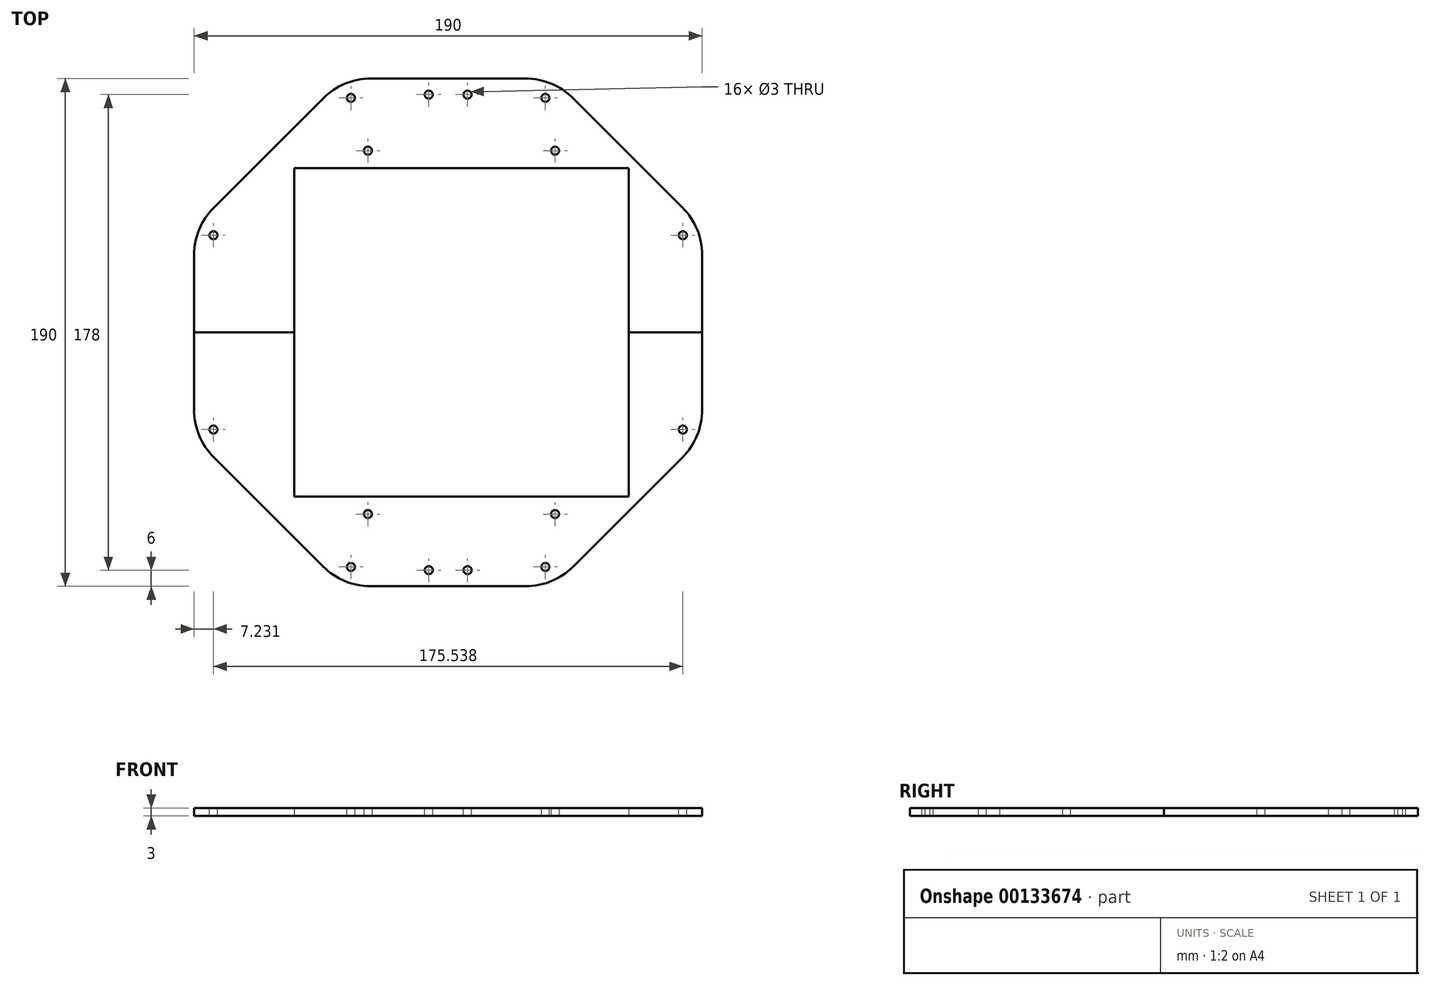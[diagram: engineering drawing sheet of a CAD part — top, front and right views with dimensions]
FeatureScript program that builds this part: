
annotation { "Feature Type Name" : "Feature", "Feature Type Description" : "" }
export const myFeature = defineFeature(function(context is Context, id is Id, definition is map)
    precondition{}
    {
        {
            var Q0;
            Q0=qCreatedBy(makeId("Top.planeOp"),FACE);
            var sketch = newSketch(context, id + "F0", { "sketchPlane" : qUnion([Q0])});
            skCircle(sketch, "E0.cCircle", {"center": v(0, 0) * mm, "radius": 95 * mm, "construction": true});
            skLineSegment(sketch, "E0.0", {"start": v(-95, -39.35) * mm, "end": v(-95, 39.35) * mm});
            skLineSegment(sketch, "E0.1", {"start": v(-95, 39.35) * mm, "end": v(-39.35, 95) * mm});
            skLineSegment(sketch, "E0.2", {"start": v(-39.35, 95) * mm, "end": v(39.35, 95) * mm});
            skLineSegment(sketch, "E0.3", {"start": v(39.35, 95) * mm, "end": v(95, 39.35) * mm});
            skLineSegment(sketch, "E0.4", {"start": v(95, 39.35) * mm, "end": v(95, -39.35) * mm});
            skLineSegment(sketch, "E0.5", {"start": v(95, -39.35) * mm, "end": v(39.35, -95) * mm});
            skLineSegment(sketch, "E0.6", {"start": v(39.35, -95) * mm, "end": v(-39.35, -95) * mm});
            skLineSegment(sketch, "E0.7", {"start": v(-39.35, -95) * mm, "end": v(-95, -39.35) * mm});
            skPoint(sketch, "E0.0.midPoint", {"position": v(-95, 0) * mm});
            skLineSegment(sketch, "E1.0", {"start": v(-91, -37.7) * mm, "end": v(-91, 37.7) * mm});
            skLineSegment(sketch, "E1.1", {"start": v(-37.7, -91) * mm, "end": v(-91, -37.7) * mm});
            skLineSegment(sketch, "E1.2", {"start": v(-91, 37.7) * mm, "end": v(-37.7, 91) * mm});
            skLineSegment(sketch, "E1.3", {"start": v(37.7, -91) * mm, "end": v(-37.7, -91) * mm});
            skLineSegment(sketch, "E1.4", {"start": v(-37.7, 91) * mm, "end": v(37.7, 91) * mm});
            skLineSegment(sketch, "E1.5", {"start": v(37.7, 91) * mm, "end": v(91, 37.7) * mm});
            skLineSegment(sketch, "E1.6", {"start": v(91, 37.7) * mm, "end": v(91, -37.7) * mm});
            skLineSegment(sketch, "E1.7", {"start": v(91, -37.7) * mm, "end": v(37.7, -91) * mm});
            skLineSegment(sketch, "E2", {"start": v(0, 91) * mm, "end": v(0, 95) * mm});
            skLineSegment(sketch, "E3", {"start": v(-95, 0) * mm, "end": v(95, 0) * mm});
            skLineSegment(sketch, "E4", {"start": v(0, -91) * mm, "end": v(0, -95) * mm});
            skCircle(sketch, "E5", {"center": v(-87.77, 36.36) * mm, "radius": 1.5 * mm});
            skCircle(sketch, "E6", {"center": v(-7.25, 89) * mm, "radius": 1.5 * mm});
            skCircle(sketch, "E7", {"center": v(7.25, 89) * mm, "radius": 1.5 * mm});
            skLineSegment(sketch, "E8", {"start": v(0, 0) * mm, "end": v(-95, 39.35) * mm, "construction": true});
            skLineSegment(sketch, "E9", {"start": v(0, 0) * mm, "end": v(0, 89) * mm, "construction": true});
            skLineSegment(sketch, "E10", {"start": v(-7.25, 89) * mm, "end": v(0, 89) * mm, "construction": true});
            skLineSegment(sketch, "E11", {"start": v(7.25, 89) * mm, "end": v(0, 89) * mm, "construction": true});
            skArc(sketch, "E12", {"start": v(-15.77, 91) * mm, "mid": v(-7.25, 85.59) * mm, "end": v(1.27, 91) * mm});
            skArc(sketch, "E13", {"start": v(-1.27, 91) * mm, "mid": v(7.25, 85.59) * mm, "end": v(15.77, 91) * mm});
            skLineSegment(sketch, "E14", {"start": v(0, 89) * mm, "end": v(0, 91) * mm});
            skArc(sketch, "E15.1.0", {"start": v(15.77, -91) * mm, "mid": v(7.25, -85.59) * mm, "end": v(-1.27, -91) * mm});
            skCircle(sketch, "E15.1.1", {"center": v(7.25, -89) * mm, "radius": 1.5 * mm});
            skArc(sketch, "E15.1.2", {"start": v(1.27, -91) * mm, "mid": v(-7.25, -85.59) * mm, "end": v(-15.77, -91) * mm});
            skCircle(sketch, "E15.1.3", {"center": v(-7.25, -89) * mm, "radius": 1.5 * mm});
            skLineSegment(sketch, "E15.1.4", {"start": v(0, -89) * mm, "end": v(0, -91) * mm});
            skArc(sketch, "E16.trimOffspring", {"start": v(-91, 28) * mm, "mid": v(-83.89, 34.75) * mm, "end": v(-84.15, 44.54) * mm});
            skCircle(sketch, "E17.1.0", {"center": v(-87.77, -36.35) * mm, "radius": 1.5 * mm});
            skArc(sketch, "E17.1.1", {"start": v(-84.15, -44.54) * mm, "mid": v(-83.89, -34.75) * mm, "end": v(-91, -28) * mm});
            skCircle(sketch, "E17.2.0", {"center": v(-36.36, -87.77) * mm, "radius": 1.5 * mm});
            skArc(sketch, "E17.2.1", {"start": v(-28, -91) * mm, "mid": v(-34.75, -83.89) * mm, "end": v(-44.54, -84.15) * mm});
            skCircle(sketch, "E17.3.0", {"center": v(36.36, -87.77) * mm, "radius": 1.5 * mm});
            skArc(sketch, "E17.3.1", {"start": v(44.54, -84.15) * mm, "mid": v(34.75, -83.89) * mm, "end": v(28, -91) * mm});
            skCircle(sketch, "E17.4.0", {"center": v(87.77, -36.36) * mm, "radius": 1.5 * mm});
            skArc(sketch, "E17.4.1", {"start": v(91, -28) * mm, "mid": v(83.89, -34.75) * mm, "end": v(84.15, -44.54) * mm});
            skCircle(sketch, "E17.5.0", {"center": v(87.77, 36.35) * mm, "radius": 1.5 * mm});
            skArc(sketch, "E17.5.1", {"start": v(84.15, 44.54) * mm, "mid": v(83.89, 34.75) * mm, "end": v(91, 28) * mm});
            skCircle(sketch, "E17.6.0", {"center": v(36.36, 87.77) * mm, "radius": 1.5 * mm});
            skArc(sketch, "E17.6.1", {"start": v(28, 91) * mm, "mid": v(34.75, 83.89) * mm, "end": v(44.54, 84.15) * mm});
            skCircle(sketch, "E17.7.0", {"center": v(-36.35, 87.77) * mm, "radius": 1.5 * mm});
            skArc(sketch, "E17.7.1", {"start": v(-44.54, 84.15) * mm, "mid": v(-34.75, 83.89) * mm, "end": v(-28, 91) * mm});
            skSolve(sketch);
        }
        {
            var Q0;
            Q0=makeQuery(id+"F0.imprint","IMPRINT",FACE,{"disambiguationData":[TD([[makeQuery(id+"F0.imprint","IMPRINT",EDGE,{"derivedFrom":sQuery(id+"F0.wireOp",EDGE,"E6")}),-1.0]])]});
            var Q1;
            Q1=makeQuery(id+"F0.imprint","IMPRINT",FACE,{"disambiguationData":[TD([[makeQuery(id+"F0.imprint","IMPRINT",EDGE,{"derivedFrom":sQuery(id+"F0.wireOp",EDGE,"E7")}),-1.0]])]});
            var Q2;
            {var subQ0=sQuery(id+"F0.wireOp",EDGE,"E14");Q2=makeQuery(id+"F0.imprint","IMPRINT",FACE,{"disambiguationData":[TD([[makeQuery(id+"F0.imprint","IMPRINT",EDGE,{"derivedFrom":subQ0}),-1.0]])]});}
            var Q3;
            {var subQ0=sQuery(id+"F0.wireOp",EDGE,"E14");Q3=makeQuery(id+"F0.imprint","IMPRINT",FACE,{"disambiguationData":[TD([[makeQuery(id+"F0.imprint","IMPRINT",EDGE,{"derivedFrom":subQ0}),1.0]])]});}
            var Q4;
            {var subQ11=sQuery(id+"F0.wireOp",EDGE,"E1.2");Q4=makeQuery(id+"F0.imprint","IMPRINT",FACE,{"disambiguationData":[TD([[makeQuery(id+"F0.imprint","IMPRINT",EDGE,{"derivedFrom":subQ11}),-1.0]])]});}
            var Q5;
            {var subQ8=sQuery(id+"F0.wireOp",EDGE,"E0.1");Q5=makeQuery(id+"F0.imprint","IMPRINT",FACE,{"disambiguationData":[TD([[makeQuery(id+"F0.imprint","IMPRINT",EDGE,{"derivedFrom":subQ8}),-1.0]])]});}
            var Q6;
            {var subQ4=sQuery(id+"F0.wireOp",EDGE,"E0.3");Q6=makeQuery(id+"F0.imprint","IMPRINT",FACE,{"disambiguationData":[TD([[makeQuery(id+"F0.imprint","IMPRINT",EDGE,{"derivedFrom":subQ4}),-1.0]])]});}
            var Q7;
            Q7=makeQuery(id+"F0.imprint","IMPRINT",FACE,{"disambiguationData":[TD([[makeQuery(id+"F0.imprint","IMPRINT",EDGE,{"derivedFrom":sQuery(id+"F0.wireOp",EDGE,"E17.5.0")}),-1.0]])]});
            var Q8;
            Q8=makeQuery(id+"F0.imprint","IMPRINT",FACE,{"disambiguationData":[TD([[makeQuery(id+"F0.imprint","IMPRINT",EDGE,{"derivedFrom":sQuery(id+"F0.wireOp",EDGE,"E17.6.0")}),-1.0]])]});
            var Q9;
            {var subQ15=sQuery(id+"F0.wireOp",EDGE,"E16.trimOffspring");Q9=makeQuery(id+"F0.imprint","IMPRINT",FACE,{"disambiguationData":[TD([[makeQuery(id+"F0.imprint","IMPRINT",EDGE,{"derivedFrom":subQ15}),-1.0]])]});}
            extrude(context, id + "F1", {"entities" : qUnion([Q0, Q1, Q2, Q3, Q4, Q5, Q6, Q7, Q8, Q9]), "oppositeDirection" : true, "depth" : 3 * mm});
        }
        {
            var Q0;
            Q0=makeQuery(id+"F0.imprint","IMPRINT",FACE,{"disambiguationData":[TD([[makeQuery(id+"F0.imprint","IMPRINT",EDGE,{"derivedFrom":sQuery(id+"F0.wireOp",EDGE,"E17.1.0")}),-1.0]])]});
            var Q1;
            Q1=makeQuery(id+"F0.imprint","IMPRINT",FACE,{"disambiguationData":[TD([[makeQuery(id+"F0.imprint","IMPRINT",EDGE,{"derivedFrom":sQuery(id+"F0.wireOp",EDGE,"E17.4.0")}),-1.0]])]});
            var Q2;
            Q2=makeQuery(id+"F0.imprint","IMPRINT",FACE,{"disambiguationData":[TD([[makeQuery(id+"F0.imprint","IMPRINT",EDGE,{"derivedFrom":sQuery(id+"F0.wireOp",EDGE,"E17.3.0")}),-1.0]])]});
            var Q3;
            Q3=makeQuery(id+"F0.imprint","IMPRINT",FACE,{"disambiguationData":[TD([[makeQuery(id+"F0.imprint","IMPRINT",EDGE,{"derivedFrom":sQuery(id+"F0.wireOp",EDGE,"E15.1.1")}),-1.0]])]});
            var Q4;
            Q4=makeQuery(id+"F0.imprint","IMPRINT",FACE,{"disambiguationData":[TD([[makeQuery(id+"F0.imprint","IMPRINT",EDGE,{"derivedFrom":sQuery(id+"F0.wireOp",EDGE,"E15.1.3")}),-1.0]])]});
            var Q5;
            Q5=makeQuery(id+"F0.imprint","IMPRINT",FACE,{"disambiguationData":[TD([[makeQuery(id+"F0.imprint","IMPRINT",EDGE,{"derivedFrom":sQuery(id+"F0.wireOp",EDGE,"E17.2.0")}),-1.0]])]});
            var Q6;
            {var subQ2=sQuery(id+"F0.wireOp",EDGE,"E15.1.4");Q6=makeQuery(id+"F0.imprint","IMPRINT",FACE,{"disambiguationData":[TD([[makeQuery(id+"F0.imprint","IMPRINT",EDGE,{"derivedFrom":subQ2}),-1.0]])]});}
            var Q7;
            {var subQ3=sQuery(id+"F0.wireOp",EDGE,"E15.1.4");Q7=makeQuery(id+"F0.imprint","IMPRINT",FACE,{"disambiguationData":[TD([[makeQuery(id+"F0.imprint","IMPRINT",EDGE,{"derivedFrom":subQ3}),1.0]])]});}
            var Q8;
            {var subQ0=sQuery(id+"F0.wireOp",EDGE,"E17.1.1");Q8=makeQuery(id+"F0.imprint","IMPRINT",FACE,{"disambiguationData":[TD([[makeQuery(id+"F0.imprint","IMPRINT",EDGE,{"derivedFrom":subQ0}),-1.0]])]});}
            var Q9;
            {var subQ16=sQuery(id+"F0.wireOp",EDGE,"E0.5");Q9=makeQuery(id+"F0.imprint","IMPRINT",FACE,{"disambiguationData":[TD([[makeQuery(id+"F0.imprint","IMPRINT",EDGE,{"derivedFrom":subQ16}),-1.0]])]});}
            var Q10;
            {var subQ9=sQuery(id+"F0.wireOp",EDGE,"E0.7");Q10=makeQuery(id+"F0.imprint","IMPRINT",FACE,{"disambiguationData":[TD([[makeQuery(id+"F0.imprint","IMPRINT",EDGE,{"derivedFrom":subQ9}),-1.0]])]});}
            extrude(context, id + "F2", {"entities" : qUnion([Q0, Q1, Q2, Q3, Q4, Q5, Q6, Q7, Q8, Q9, Q10]), "oppositeDirection" : true, "depth" : 3 * mm});
        }
        {
            var Q0;
            Q0=makeQuery(id+"F2.opExtrude","CAP_FACE",FACE,{"disambiguationData":[OSD([sQuery(id+"F0.wireOp",EDGE,"E0.0"),sQuery(id+"F0.wireOp",EDGE,"E0.1"),sQuery(id+"F0.wireOp",EDGE,"E0.2"),sQuery(id+"F0.wireOp",EDGE,"E0.3"),sQuery(id+"F0.wireOp",EDGE,"E0.4"),sQuery(id+"F0.wireOp",EDGE,"E3")])],"isStart":false});
            var sketch = newSketch(context, id + "F3", { "sketchPlane" : qUnion([Q0])});
            skLineSegment(sketch, "E18.bottom", {"start": v(40, 68) * mm, "end": v(-30, 68) * mm, "construction": true});
            skLineSegment(sketch, "E18.top", {"start": v(40, -68) * mm, "end": v(-30, -68) * mm, "construction": true});
            skLineSegment(sketch, "E18.left", {"start": v(40, 68) * mm, "end": v(40, -68) * mm, "construction": true});
            skLineSegment(sketch, "E18.right", {"start": v(-30, 68) * mm, "end": v(-30, -68) * mm, "construction": true});
            skPoint(sketch, "E18.middle", {"position": v(0, 0) * mm});
            skCircle(sketch, "E19", {"center": v(-30, 68) * mm, "radius": 1.5 * mm});
            skCircle(sketch, "E20", {"center": v(40, 68) * mm, "radius": 1.5 * mm});
            skCircle(sketch, "E21", {"center": v(40, -68) * mm, "radius": 1.5 * mm});
            skCircle(sketch, "E22", {"center": v(-30, -68) * mm, "radius": 1.5 * mm});
            skLineSegment(sketch, "E23", {"start": v(0, 0) * mm, "end": v(5, 0) * mm});
            skLineSegment(sketch, "E24.bottom", {"start": v(-57.5, 61.5) * mm, "end": v(67.5, 61.5) * mm});
            skLineSegment(sketch, "E24.top", {"start": v(-57.5, -61.5) * mm, "end": v(67.5, -61.5) * mm});
            skLineSegment(sketch, "E24.left", {"start": v(-57.5, 61.5) * mm, "end": v(-57.5, -61.5) * mm});
            skLineSegment(sketch, "E24.right", {"start": v(67.5, 61.5) * mm, "end": v(67.5, -61.5) * mm});
            skPoint(sketch, "E24.middle", {"position": v(5, 0) * mm});
            skPoint(sketch, "E25.positionSnap0", {"position": v(5, -68) * mm});
            skPoint(sketch, "E25.positionSnap1", {"position": v(-30, 0) * mm});
            skSolve(sketch);
        }
        {
            var Q0;
            Q0=qSketchRegion(id+"F3",true);
            extrude(context, id + "F4", {"entities" : qUnion([Q0]), "operationType" : NewBodyOperationType.REMOVE, "oppositeDirection" : true, "depth" : 25 * mm});
        }
        {
            var Q0;
            Q0=makeQuery(id+"F2.opExtrude","SWEPT_EDGE",EDGE,{"disambiguationData":[OSD([sQuery(id+"F0.wireOp",EDGE,"E0.5"),sQuery(id+"F0.wireOp",EDGE,"E0.6")])]});
            var Q1;
            Q1=makeQuery(id+"F2.opExtrude","SWEPT_EDGE",EDGE,{"disambiguationData":[OSD([sQuery(id+"F0.wireOp",EDGE,"E0.6"),sQuery(id+"F0.wireOp",EDGE,"E0.7")])]});
            var Q2;
            Q2=makeQuery(id+"F2.opExtrude","SWEPT_EDGE",EDGE,{"disambiguationData":[OSD([sQuery(id+"F0.wireOp",EDGE,"E0.0"),sQuery(id+"F0.wireOp",EDGE,"E0.7")])]});
            var Q3;
            Q3=makeQuery(id+"F1.opExtrude","SWEPT_EDGE",EDGE,{"disambiguationData":[OSD([sQuery(id+"F0.wireOp",EDGE,"E0.0"),sQuery(id+"F0.wireOp",EDGE,"E0.1")])]});
            var Q4;
            Q4=makeQuery(id+"F1.opExtrude","SWEPT_EDGE",EDGE,{"disambiguationData":[OSD([sQuery(id+"F0.wireOp",EDGE,"E0.1"),sQuery(id+"F0.wireOp",EDGE,"E0.2")])]});
            var Q5;
            Q5=makeQuery(id+"F1.opExtrude","SWEPT_EDGE",EDGE,{"disambiguationData":[OSD([sQuery(id+"F0.wireOp",EDGE,"E0.2"),sQuery(id+"F0.wireOp",EDGE,"E0.3")])]});
            var Q6;
            Q6=makeQuery(id+"F1.opExtrude","SWEPT_EDGE",EDGE,{"disambiguationData":[OSD([sQuery(id+"F0.wireOp",EDGE,"E0.3"),sQuery(id+"F0.wireOp",EDGE,"E0.4")])]});
            var Q7;
            Q7=makeQuery(id+"F2.opExtrude","SWEPT_EDGE",EDGE,{"disambiguationData":[OSD([sQuery(id+"F0.wireOp",EDGE,"E0.4"),sQuery(id+"F0.wireOp",EDGE,"E0.5")])]});
            fillet(context, id + "F5", {"entities" : qUnion([Q0, Q1, Q2, Q3, Q4, Q5, Q6, Q7]), "radius" : 25 * mm, "tangentPropagation" : true, "allowEdgeOverflow" : false});
        }
    });
